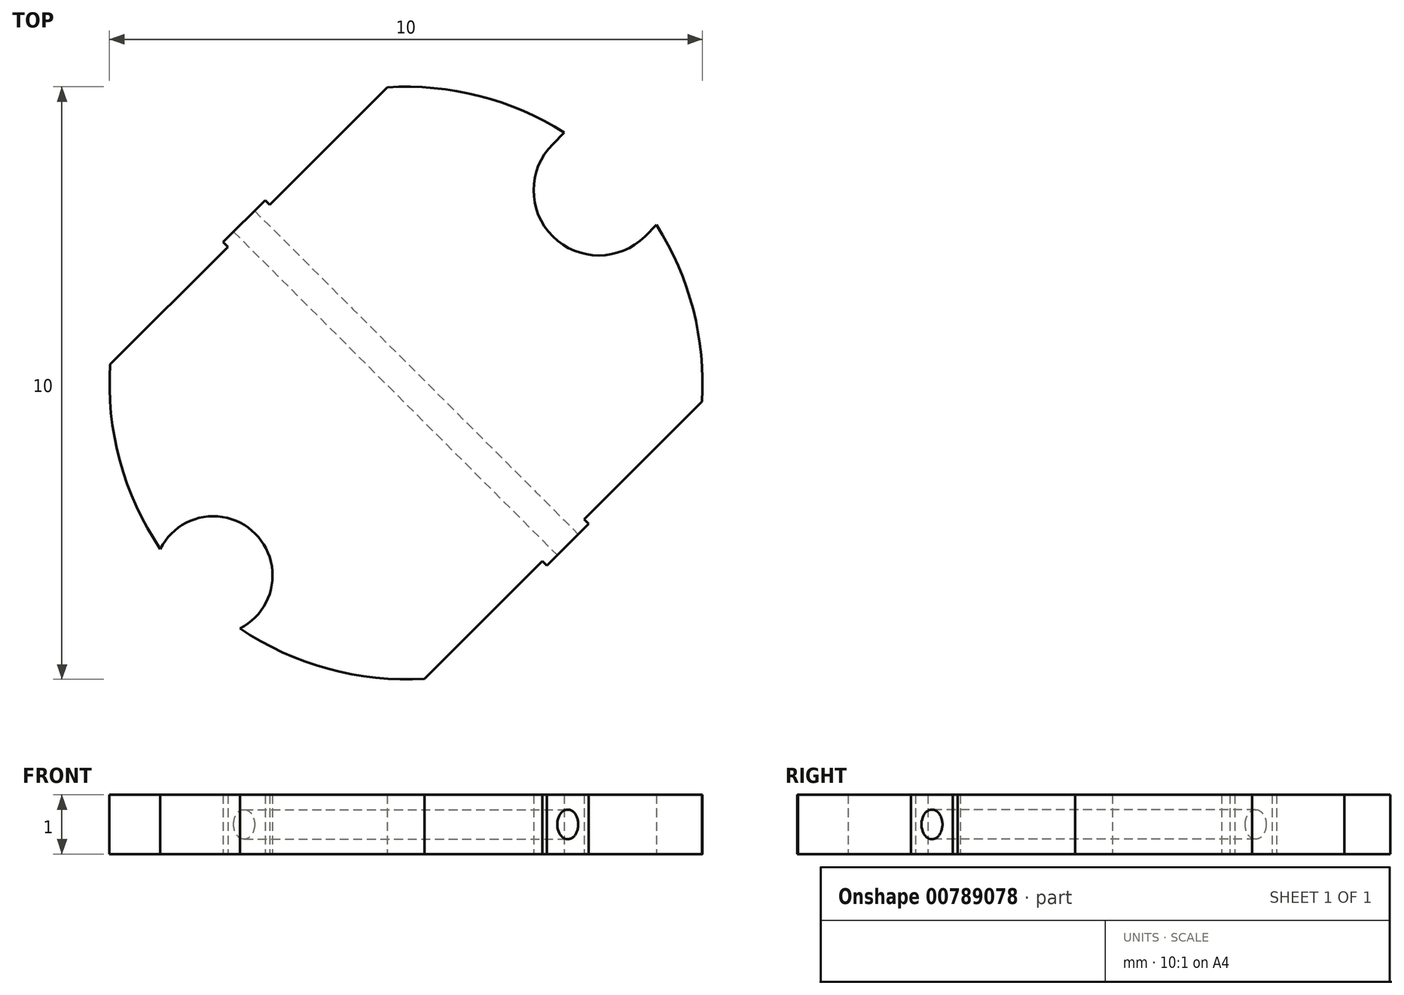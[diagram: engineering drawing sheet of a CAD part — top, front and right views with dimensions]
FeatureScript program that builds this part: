
annotation { "Feature Type Name" : "Feature", "Feature Type Description" : "" }
export const myFeature = defineFeature(function(context is Context, id is Id, definition is map)
    precondition{}
    {
        {
            var Q0;
            Q0=qCreatedBy(makeId("Top.planeOp"),FACE);
            var sketch = newSketch(context, id + "F0", { "sketchPlane" : qUnion([Q0])});
            skArc(sketch, "E0", {"start": v(-5, 0.31) * mm, "mid": v(-4.82, -1.31) * mm, "end": v(-4.14, -2.8) * mm});
            skLineSegment(sketch, "E1.bottom", {"start": v(5, -5) * mm, "end": v(-5, -5) * mm, "construction": true});
            skLineSegment(sketch, "E1.top", {"start": v(5, 5) * mm, "end": v(-5, 5) * mm, "construction": true});
            skLineSegment(sketch, "E1.left", {"start": v(5, -5) * mm, "end": v(5, 5) * mm, "construction": true});
            skLineSegment(sketch, "E1.right", {"start": v(-5, -5) * mm, "end": v(-5, 5) * mm, "construction": true});
            skLineSegment(sketch, "E2", {"start": v(-2.38, 3.08) * mm, "end": v(-2.3, 3) * mm});
            skLineSegment(sketch, "E3", {"start": v(2.38, -3.08) * mm, "end": v(2.3, -3) * mm});
            skLineSegment(sketch, "E4", {"start": v(-3.08, 2.38) * mm, "end": v(-2.38, 3.08) * mm});
            skLineSegment(sketch, "E5.trimOffspring", {"start": v(3, -2.3) * mm, "end": v(3.08, -2.38) * mm});
            skLineSegment(sketch, "E6.trimOffspring", {"start": v(-3, 2.3) * mm, "end": v(-3.08, 2.38) * mm});
            skArc(sketch, "E7.trimOffspring", {"start": v(5, -0.31) * mm, "mid": v(4.84, 1.24) * mm, "end": v(4.23, 2.67) * mm});
            skLineSegment(sketch, "E8.bottom", {"start": v(-5, 5) * mm, "end": v(-0.3, 5) * mm, "construction": true});
            skLineSegment(sketch, "E8.top", {"start": v(-5, 0.3) * mm, "end": v(-0.3, 0.3) * mm, "construction": true});
            skLineSegment(sketch, "E8.left", {"start": v(-5, 5) * mm, "end": v(-5, 0.3) * mm, "construction": true});
            skLineSegment(sketch, "E8.right", {"start": v(-0.3, 5) * mm, "end": v(-0.3, 0.3) * mm, "construction": true});
            skLineSegment(sketch, "E9.bottom", {"start": v(5, -5) * mm, "end": v(0.3, -5) * mm, "construction": true});
            skLineSegment(sketch, "E9.top", {"start": v(5, -0.3) * mm, "end": v(0.3, -0.3) * mm, "construction": true});
            skLineSegment(sketch, "E9.left", {"start": v(5, -5) * mm, "end": v(5, -0.3) * mm, "construction": true});
            skLineSegment(sketch, "E9.right", {"start": v(0.3, -5) * mm, "end": v(0.3, -0.3) * mm, "construction": true});
            skLineSegment(sketch, "E10", {"start": v(-0.3, 5) * mm, "end": v(-2.3, 3) * mm});
            skLineSegment(sketch, "E11", {"start": v(5, -0.3) * mm, "end": v(3, -2.3) * mm});
            skLineSegment(sketch, "E12.trimOffspring", {"start": v(2.3, -3) * mm, "end": v(0.3, -5) * mm});
            skLineSegment(sketch, "E13.trimOffspring", {"start": v(-3, 2.3) * mm, "end": v(-5, 0.3) * mm});
            skLineSegment(sketch, "E14", {"start": v(-5, 0.46) * mm, "end": v(-0.46, 5) * mm, "construction": true});
            skLineSegment(sketch, "E15", {"start": v(-0.46, 5) * mm, "end": v(-0.44, 5) * mm, "construction": true});
            skLineSegment(sketch, "E16", {"start": v(-0.44, 5) * mm, "end": v(-5, 0.44) * mm, "construction": true});
            skLineSegment(sketch, "E17", {"start": v(-5, 0.44) * mm, "end": v(-5, 0.46) * mm, "construction": true});
            skLineSegment(sketch, "E18", {"start": v(-5, -5) * mm, "end": v(5, 5) * mm, "construction": true});
            skLineSegment(sketch, "E19.MirrorCS", {"start": v(5, -0.44) * mm, "end": v(0.44, -5) * mm, "construction": true});
            skLineSegment(sketch, "E20.MirrorCS", {"start": v(0.46, -5) * mm, "end": v(5, -0.46) * mm, "construction": true});
            skLineSegment(sketch, "E21", {"start": v(2.38, -3.08) * mm, "end": v(3.08, -2.38) * mm});
            skArc(sketch, "E22", {"start": v(2.47, 4.03) * mm, "mid": v(2.47, 2.47) * mm, "end": v(4.03, 2.47) * mm});
            skLineSegment(sketch, "E23", {"start": v(2.47, 4.03) * mm, "end": v(3.25, 3.25) * mm, "construction": true});
            skLineSegment(sketch, "E24", {"start": v(4.03, 2.47) * mm, "end": v(3.25, 3.25) * mm, "construction": true});
            skLineSegment(sketch, "E25", {"start": v(4.03, 2.47) * mm, "end": v(4.23, 2.67) * mm});
            skLineSegment(sketch, "E26", {"start": v(2.47, 4.03) * mm, "end": v(2.67, 4.23) * mm});
            skArc(sketch, "E27.trimOffspring", {"start": v(2.67, 4.23) * mm, "mid": v(1.24, 4.84) * mm, "end": v(-0.31, 5) * mm});
            skLineSegment(sketch, "E28.bottom", {"start": v(3.25, -3.25) * mm, "end": v(-3.25, -3.25) * mm, "construction": true});
            skLineSegment(sketch, "E28.top", {"start": v(3.25, 3.25) * mm, "end": v(-3.25, 3.25) * mm, "construction": true});
            skLineSegment(sketch, "E28.left", {"start": v(3.25, -3.25) * mm, "end": v(3.25, 3.25) * mm, "construction": true});
            skLineSegment(sketch, "E28.right", {"start": v(-3.25, -3.25) * mm, "end": v(-3.25, 3.25) * mm, "construction": true});
            skArc(sketch, "E29", {"start": v(-2.8, -4.14) * mm, "mid": v(-2.54, -2.54) * mm, "end": v(-4.14, -2.8) * mm});
            skArc(sketch, "E30.trimOffspring", {"start": v(-2.8, -4.14) * mm, "mid": v(-1.31, -4.82) * mm, "end": v(0.31, -5) * mm});
            skSolve(sketch);
        }
        {
            var Q0;
            Q0=makeQuery(id+"F0.imprint","IMPRINT",FACE,{"disambiguationData":[TD([[makeQuery(id+"F0.imprint","IMPRINT",EDGE,{"derivedFrom":sQuery(id+"F0.wireOp",EDGE,"E0")}),1.0]])]});
            extrude(context, id + "F1", {"entities" : qUnion([Q0]), "endBound" : BoundingType.SYMMETRIC, "depth" : 1 * mm, "offsetDistance" : 25 * mm});
        }
        {
            var Q0;
            Q0=makeQuery(id+"F1.opExtrude","SWEPT_FACE",FACE,{"disambiguationData":[OSD([sQuery(id+"F0.wireOp",EDGE,"E21")])]});
            var sketch = newSketch(context, id + "F2", { "sketchPlane" : qUnion([Q0])});
            skCircle(sketch, "E31", {"center": v(0, 0) * mm, "radius": 0.25 * mm});
            skSolve(sketch);
        }
        {
            var Q0;
            Q0 = qSketchRegion(id + "F2", true);
            extrude(context, id + "F3", {"entities" : qUnion([Q0]), "operationType" : NewBodyOperationType.REMOVE, "endBound" : BoundingType.THROUGH_ALL, "oppositeDirection" : true, "depth" : 25 * mm, "offsetDistance" : 25 * mm});
        }
    });
